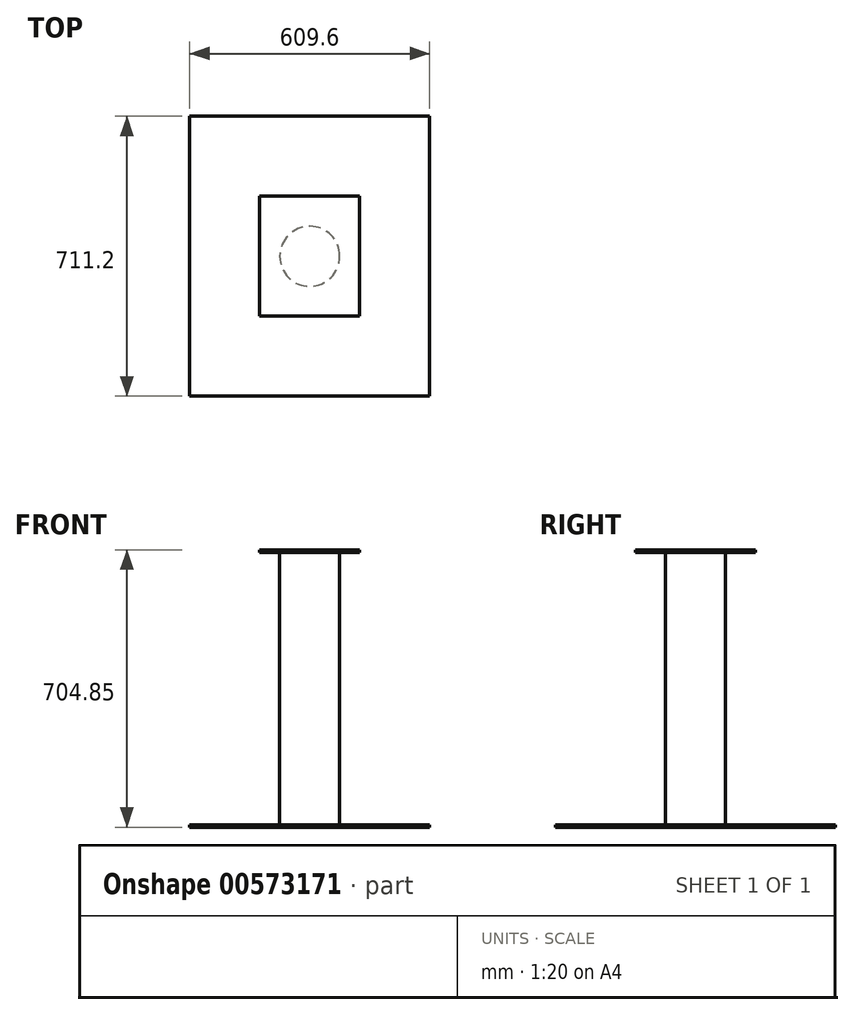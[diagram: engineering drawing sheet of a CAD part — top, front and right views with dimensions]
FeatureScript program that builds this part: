
annotation { "Feature Type Name" : "Feature", "Feature Type Description" : "" }
export const myFeature = defineFeature(function(context is Context, id is Id, definition is map)
    precondition{}
    {
        {
            var Q0;
            Q0=qCreatedBy(makeId("Top.planeOp"),FACE);
            var sketch = newSketch(context, id + "F0", { "sketchPlane" : qUnion([Q0])});
            skLineSegment(sketch, "E0.bottom", {"start": v(304.8, 355.6) * mm, "end": v(-304.8, 355.6) * mm});
            skLineSegment(sketch, "E0.top", {"start": v(304.8, -355.6) * mm, "end": v(-304.8, -355.6) * mm});
            skLineSegment(sketch, "E0.left", {"start": v(304.8, 355.6) * mm, "end": v(304.8, -355.6) * mm});
            skLineSegment(sketch, "E0.right", {"start": v(-304.8, 355.6) * mm, "end": v(-304.8, -355.6) * mm});
            skPoint(sketch, "E0.middle", {"position": v(0, 0) * mm});
            skSolve(sketch);
        }
        {
            var Q0;
            Q0=makeQuery(id+"F0.imprint","IMPRINT",FACE,{"disambiguationData":[TD([[makeQuery(id+"F0.imprint","IMPRINT",EDGE,{"derivedFrom":sQuery(id+"F0.wireOp",EDGE,"E0.bottom")}),1.0]])]});
            extrude(context, id + "F1", {"entities" : qUnion([Q0]), "depth" : 6.35 * mm, "offsetDistance" : 25.4 * mm});
        }
        {
            var Q0;
            Q0=makeQuery(id+"F1.opExtrude","CAP_FACE",FACE,{"disambiguationData":[OSD([sQuery(id+"F0.wireOp",EDGE,"E0.bottom"),sQuery(id+"F0.wireOp",EDGE,"E0.top"),sQuery(id+"F0.wireOp",EDGE,"E0.left"),sQuery(id+"F0.wireOp",EDGE,"E0.right")])],"isStart":false});
            var sketch = newSketch(context, id + "F2", { "sketchPlane" : qUnion([Q0])});
            skCircle(sketch, "E1", {"center": v(0, 0) * mm, "radius": 76.2 * mm});
            skSolve(sketch);
        }
        {
            var Q0;
            Q0=makeQuery(id+"F2.imprint","IMPRINT",FACE,{"disambiguationData":[TD([[makeQuery(id+"F2.imprint","IMPRINT",EDGE,{"derivedFrom":sQuery(id+"F2.wireOp",EDGE,"E1")}),1.0]])]});
            extrude(context, id + "F3", {"entities" : qUnion([Q0]), "operationType" : NewBodyOperationType.ADD, "depth" : 692.15 * mm, "offsetDistance" : 25.4 * mm});
        }
        {
            var Q0;
            Q0=makeQuery(id+"F3.opExtrude","CAP_FACE",FACE,{"disambiguationData":[OSD([sQuery(id+"F2.wireOp",EDGE,"E1")])],"isStart":false});
            var sketch = newSketch(context, id + "F4", { "sketchPlane" : qUnion([Q0])});
            skLineSegment(sketch, "E2.bottom", {"start": v(127, 152.4) * mm, "end": v(-127, 152.4) * mm});
            skLineSegment(sketch, "E2.top", {"start": v(127, -152.4) * mm, "end": v(-127, -152.4) * mm});
            skLineSegment(sketch, "E2.left", {"start": v(127, 152.4) * mm, "end": v(127, -152.4) * mm});
            skLineSegment(sketch, "E2.right", {"start": v(-127, 152.4) * mm, "end": v(-127, -152.4) * mm});
            skPoint(sketch, "E2.middle", {"position": v(0, 0) * mm});
            skSolve(sketch);
        }
        {
            var Q0;
            Q0=makeQuery(id+"F4.imprint","IMPRINT",FACE,{"disambiguationData":[TD([[makeQuery(id+"F4.imprint","IMPRINT",EDGE,{"derivedFrom":sQuery(id+"F4.wireOp",EDGE,"E2.bottom")}),1.0]])]});
            var Q1;
            Q1=makeQuery(id+"F4.imprint","IMPRINT",FACE,{"disambiguationData":[TD([[makeQuery(id+"F4.imprint","IMPRINT",EDGE,{"derivedFrom":makeQuery(id+"F3.opExtrude","CAP_EDGE",EDGE,{"disambiguationData":[OSD([sQuery(id+"F2.wireOp",EDGE,"E1")])],"isStart":false})}),1.0]])]});
            extrude(context, id + "F5", {"entities" : qUnion([Q0, Q1]), "operationType" : NewBodyOperationType.ADD, "depth" : 6.35 * mm, "offsetDistance" : 25.4 * mm});
        }
    });
